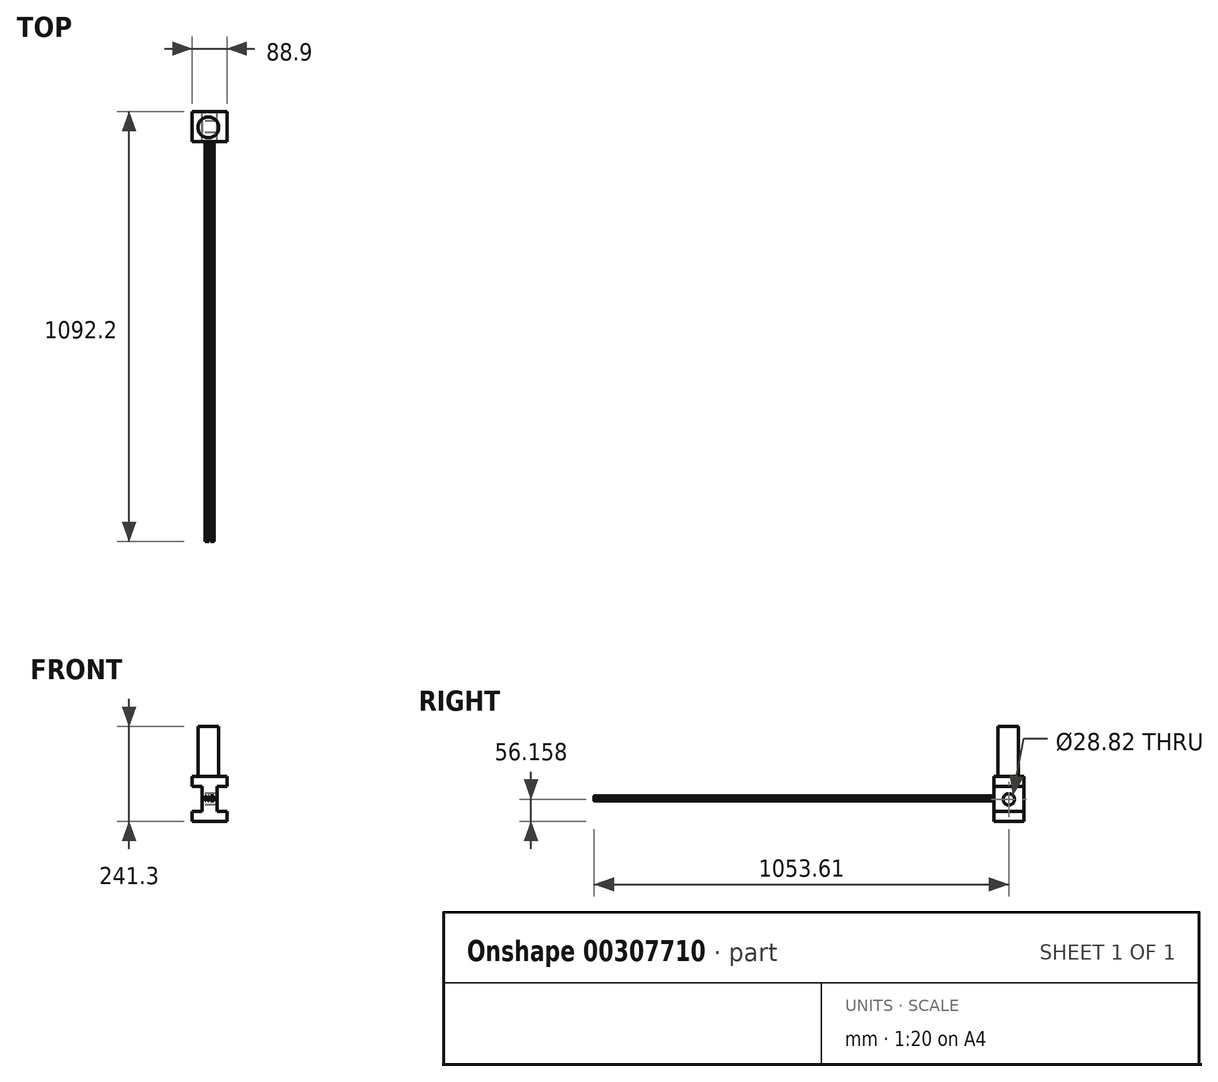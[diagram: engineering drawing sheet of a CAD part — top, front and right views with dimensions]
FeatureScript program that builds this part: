
annotation { "Feature Type Name" : "Feature", "Feature Type Description" : "" }
export const myFeature = defineFeature(function(context is Context, id is Id, definition is map)
    precondition{}
    {
        {
            var Q0;
            Q0=qCreatedBy(makeId("Front.planeOp"),FACE);
            var sketch = newSketch(context, id + "F0", { "sketchPlane" : qUnion([Q0])});
            skLineSegment(sketch, "E0", {"start": v(-41.33, -52) * mm, "end": v(47.57, -52) * mm});
            skLineSegment(sketch, "E1", {"start": v(47.57, -52) * mm, "end": v(47.57, -26.6) * mm});
            skLineSegment(sketch, "E2", {"start": v(47.57, -26.6) * mm, "end": v(22.17, -26.6) * mm});
            skLineSegment(sketch, "E3", {"start": v(22.17, -26.6) * mm, "end": v(22.17, 36.9) * mm});
            skLineSegment(sketch, "E4", {"start": v(22.17, 36.9) * mm, "end": v(47.57, 36.9) * mm});
            skLineSegment(sketch, "E5", {"start": v(47.57, 36.9) * mm, "end": v(47.57, 62.3) * mm});
            skLineSegment(sketch, "E6", {"start": v(47.57, 62.3) * mm, "end": v(-41.33, 62.3) * mm});
            skLineSegment(sketch, "E7", {"start": v(-41.33, 62.3) * mm, "end": v(-41.33, 36.9) * mm});
            skLineSegment(sketch, "E8", {"start": v(-41.33, 36.9) * mm, "end": v(-15.93, 36.9) * mm});
            skLineSegment(sketch, "E9", {"start": v(-41.33, -52) * mm, "end": v(-41.33, -26.6) * mm});
            skLineSegment(sketch, "E10", {"start": v(-41.33, -26.6) * mm, "end": v(-15.93, -26.6) * mm});
            skLineSegment(sketch, "E11", {"start": v(-15.93, -26.6) * mm, "end": v(-15.93, 36.9) * mm});
            skSolve(sketch);
        }
        {
            var Q0;
            Q0=makeQuery(id+"F0.imprint","IMPRINT",FACE,{"disambiguationData":[TD([[makeQuery(id+"F0.imprint","IMPRINT",EDGE,{"derivedFrom":sQuery(id+"F0.wireOp",EDGE,"E0")}),1.0]])]});
            extrude(context, id + "F1", {"entities" : qUnion([Q0]), "depth" : 76.2 * mm});
        }
        {
            var Q0;
            Q0=makeQuery(id+"F1.opExtrude","SWEPT_FACE",FACE,{"disambiguationData":[OSD([sQuery(id+"F0.wireOp",EDGE,"E11")])]});
            var sketch = newSketch(context, id + "F2", { "sketchPlane" : qUnion([Q0])});
            skCircle(sketch, "E12", {"center": v(38.6, 4.16) * mm, "radius": 14.41 * mm});
            skPoint(sketch, "E12.first.point", {"position": v(27.86, 13.77) * mm});
            skPoint(sketch, "E12.second.point", {"position": v(50.76, -3.56) * mm});
            skPoint(sketch, "E12.third.point", {"position": v(52, 9.44) * mm});
            skSolve(sketch);
        }
        {
            var Q0;
            Q0=makeQuery(id+"F2.imprint","IMPRINT",FACE,{"disambiguationData":[TD([[makeQuery(id+"F2.imprint","IMPRINT",EDGE,{"derivedFrom":sQuery(id+"F2.wireOp",EDGE,"E12")}),1.0]])]});
            extrude(context, id + "F3", {"entities" : qUnion([Q0]), "operationType" : NewBodyOperationType.REMOVE, "oppositeDirection" : true, "depth" : 25.4 * mm});
        }
        {
            var Q0;
            Q0=makeQuery(id+"F3.boolean.opBoolean","COPY",FACE,{"derivedFrom":makeQuery(id+"F3.opExtrude","CAP_FACE",FACE,{"disambiguationData":[OSD([sQuery(id+"F2.wireOp",EDGE,"E12")])],"isStart":false})});
            extrude(context, id + "F4", {"entities" : qUnion([Q0]), "operationType" : NewBodyOperationType.REMOVE, "oppositeDirection" : true, "depth" : 25.4 * mm});
        }
        {
            var Q0;
            Q0=makeQuery(id+"F1.opExtrude","SWEPT_FACE",FACE,{"disambiguationData":[OSD([sQuery(id+"F0.wireOp",EDGE,"E6")])]});
            var sketch = newSketch(context, id + "F5", { "sketchPlane" : qUnion([Q0])});
            skCircle(sketch, "E13", {"center": v(0, -40.24) * mm, "radius": 26.4 * mm});
            skSolve(sketch);
        }
        {
            var Q0;
            Q0=makeQuery(id+"F5.imprint","IMPRINT",FACE,{"disambiguationData":[TD([[makeQuery(id+"F5.imprint","IMPRINT",EDGE,{"derivedFrom":sQuery(id+"F5.wireOp",EDGE,"E13")}),1.0]])]});
            extrude(context, id + "F6", {"entities" : qUnion([Q0]), "operationType" : NewBodyOperationType.ADD, "depth" : 127 * mm});
        }
        {
            var Q0;
            Q0=makeQuery(id+"F1.opExtrude","CAP_FACE",FACE,{"disambiguationData":[OSD([sQuery(id+"F0.wireOp",EDGE,"E0"),sQuery(id+"F0.wireOp",EDGE,"E1"),sQuery(id+"F0.wireOp",EDGE,"E2"),sQuery(id+"F0.wireOp",EDGE,"E3"),sQuery(id+"F0.wireOp",EDGE,"E4"),sQuery(id+"F0.wireOp",EDGE,"E5"),sQuery(id+"F0.wireOp",EDGE,"E6"),sQuery(id+"F0.wireOp",EDGE,"E7"),sQuery(id+"F0.wireOp",EDGE,"E8"),sQuery(id+"F0.wireOp",EDGE,"E9"),sQuery(id+"F0.wireOp",EDGE,"E10"),sQuery(id+"F0.wireOp",EDGE,"E11")])],"isStart":false});
            var sketch = newSketch(context, id + "F7", { "sketchPlane" : qUnion([Q0])});
            skText(sketch, "E14", { "text": "NB", "fontName": "OpenSans-Regular.ttf"});
            const initialGuessF7  = {"E14": [-0.01023, 0, 1, 0, 0.01311]};
            skSetInitialGuess(sketch, initialGuessF7);
            skSolve(sketch);
        }
        {
            var Q0;
            Q0 = qSketchRegion(id + "F7", true);
            extrude(context, id + "F8", {"entities" : qUnion([Q0]), "operationType" : NewBodyOperationType.ADD, "depth" : 1016 * mm});
        }
    });
